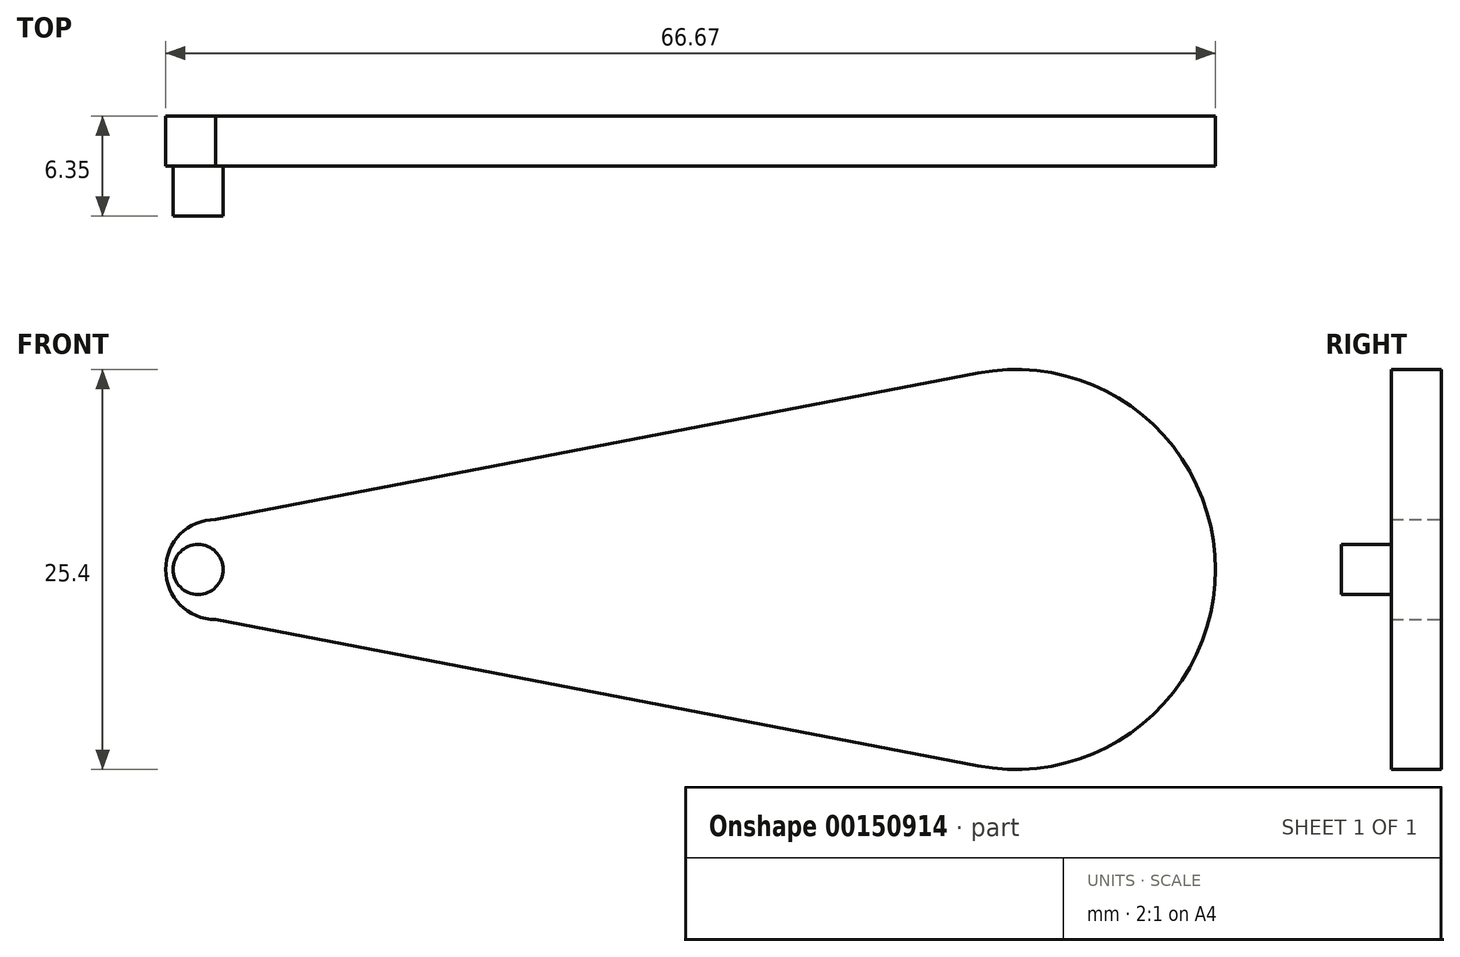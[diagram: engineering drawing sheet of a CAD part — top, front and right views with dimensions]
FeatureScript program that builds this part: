
annotation { "Feature Type Name" : "Feature", "Feature Type Description" : "" }
export const myFeature = defineFeature(function(context is Context, id is Id, definition is map)
    precondition{}
    {
        {
            var Q0;
            Q0=qCreatedBy(makeId("Front.planeOp"),FACE);
            var sketch = newSketch(context, id + "F0", { "sketchPlane" : qUnion([Q0])});
            skArc(sketch, "E0", {"start": v(-28.1, 3.18) * mm, "mid": v(-31.27, 0) * mm, "end": v(-28.1, -3.18) * mm});
            skArc(sketch, "E1", {"start": v(20.3, -12.47) * mm, "mid": v(35.4, 0) * mm, "end": v(20.3, 12.47) * mm});
            skLineSegment(sketch, "E2", {"start": v(-28.1, 3.18) * mm, "end": v(20.3, 12.47) * mm});
            skLineSegment(sketch, "E3", {"start": v(-28.1, -3.17) * mm, "end": v(20.3, -12.47) * mm});
            skPoint(sketch, "E4.orphan", {"position": v(22.7, -12.93) * mm});
            skSolve(sketch);
        }
        {
            var Q0;
            Q0=makeQuery(id+"F0.imprint","IMPRINT",FACE,{"disambiguationData":[TD([[makeQuery(id+"F0.imprint","IMPRINT",EDGE,{"derivedFrom":sQuery(id+"F0.wireOp",EDGE,"E0")}),1.0]])]});
            extrude(context, id + "F1", {"entities" : qUnion([Q0]), "depth" : 3.17 * mm});
        }
        {
            var Q0;
            Q0=makeQuery(id+"F1.opExtrude","CAP_FACE",FACE,{"disambiguationData":[OSD([sQuery(id+"F0.wireOp",EDGE,"E0"),sQuery(id+"F0.wireOp",EDGE,"E1"),sQuery(id+"F0.wireOp",EDGE,"E2"),sQuery(id+"F0.wireOp",EDGE,"E3")])],"isStart":false});
            var sketch = newSketch(context, id + "F2", { "sketchPlane" : qUnion([Q0])});
            skCircle(sketch, "E5", {"center": v(-29.21, 0) * mm, "radius": 1.59 * mm});
            skPoint(sketch, "E5.centerSnap0", {"position": v(-31.27, 0) * mm});
            skSolve(sketch);
        }
        {
            var Q0;
            Q0=makeQuery(id+"F2.imprint","IMPRINT",FACE,{"disambiguationData":[TD([[makeQuery(id+"F2.imprint","IMPRINT",EDGE,{"derivedFrom":sQuery(id+"F2.wireOp",EDGE,"E5")}),1.0]])]});
            extrude(context, id + "F3", {"entities" : qUnion([Q0]), "operationType" : NewBodyOperationType.ADD, "depth" : 3.17 * mm});
        }
    });
